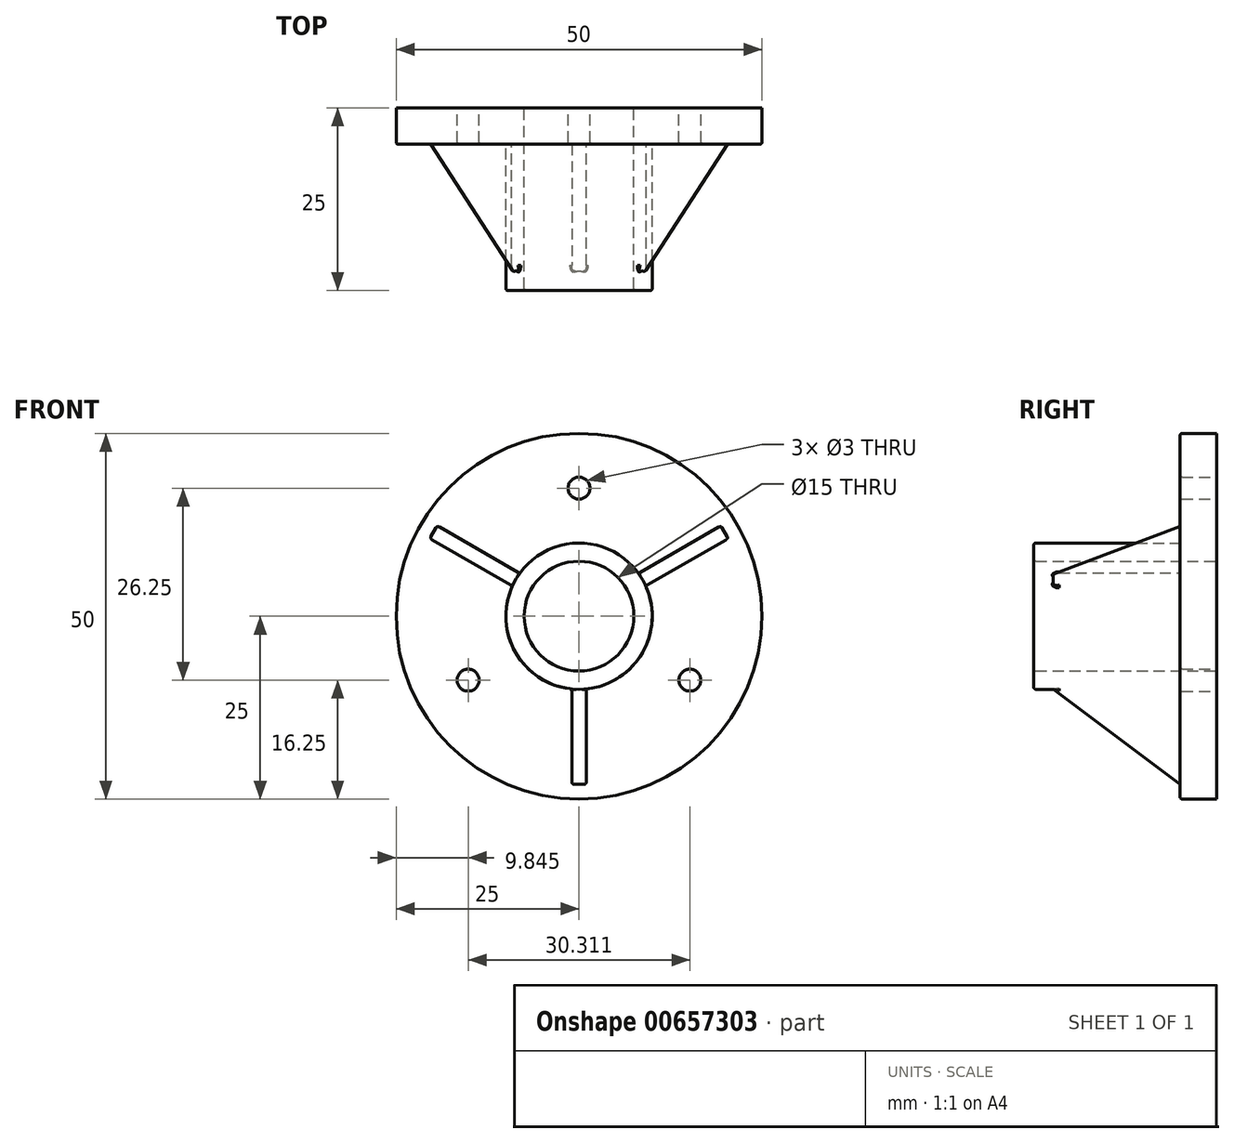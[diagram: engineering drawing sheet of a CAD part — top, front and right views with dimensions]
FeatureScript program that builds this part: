
annotation { "Feature Type Name" : "Feature", "Feature Type Description" : "" }
export const myFeature = defineFeature(function(context is Context, id is Id, definition is map)
    precondition{}
    {
        {
            var Q0;
            Q0=qCreatedBy(makeId("Front.planeOp"),FACE);
            var sketch = newSketch(context, id + "F0", { "sketchPlane" : qUnion([Q0])});
            skCircle(sketch, "E0", {"center": v(0, 0) * mm, "radius": 25 * mm});
            skCircle(sketch, "E1", {"center": v(0, 0) * mm, "radius": 10 * mm});
            skCircle(sketch, "E2", {"center": v(0, 17.5) * mm, "radius": 1.5 * mm});
            skCircle(sketch, "E3.1.0", {"center": v(-15.16, -8.75) * mm, "radius": 1.5 * mm});
            skCircle(sketch, "E3.2.0", {"center": v(15.16, -8.75) * mm, "radius": 1.5 * mm});
            skCircle(sketch, "E4", {"center": v(0, 0) * mm, "radius": 7.5 * mm});
            skSolve(sketch);
        }
        {
            var Q0;
            Q0 = qSketchRegion(id + "F0", true);
            extrude(context, id + "F1", {"entities" : qUnion([Q0]), "depth" : 5 * mm, "offsetDistance" : 25 * mm});
        }
        {
            var Q0;
            Q0=makeQuery(id+"F0.imprint","IMPRINT",FACE,{"disambiguationData":[TD([[makeQuery(id+"F0.imprint","IMPRINT",EDGE,{"derivedFrom":sQuery(id+"F0.wireOp",EDGE,"E1")}),1.0]])]});
            extrude(context, id + "F2", {"entities" : qUnion([Q0]), "operationType" : NewBodyOperationType.ADD, "depth" : 25 * mm, "offsetDistance" : 25 * mm});
        }
        {
            var Q0;
            Q0=qCreatedBy(makeId("Right.planeOp"),FACE);
            var sketch = newSketch(context, id + "F3", { "sketchPlane" : qUnion([Q0])});
            skLineSegment(sketch, "E5", {"start": v(7.15, 0) * mm, "end": v(-29.44, 0) * mm, "construction": true});
            skLineSegment(sketch, "E6", {"start": v(-25, -8) * mm, "end": v(-5, -8) * mm});
            skLineSegment(sketch, "E7", {"start": v(-5, -8) * mm, "end": v(-5, -23) * mm});
            skLineSegment(sketch, "E8", {"start": v(-5, -23) * mm, "end": v(-25, -8) * mm});
            skSolve(sketch);
        }
        {
            var Q0;
            Q0 = qSketchRegion(id + "F3", true);
            extrude(context, id + "F4", {"entities" : qUnion([Q0]), "endBound" : BoundingType.SYMMETRIC, "depth" : 2 * mm, "offsetDistance" : 25 * mm});
        }
        {
            var Q0;
            Q0=makeQuery(id+"F4.opExtrude","SWEPT_BODY",BODY,{"disambiguationData":[OSD([sQuery(id+"F3.wireOp",EDGE,"E6"),sQuery(id+"F3.wireOp",EDGE,"E7"),sQuery(id+"F3.wireOp",EDGE,"E8")])]});
            var Q1;
            Q1=sQuery(id+"F3.wireOp",EDGE,"E5");
            circularPattern(context, id + "F5", {"entities" : qUnion([Q0]), "axis" : qUnion([Q1]), "angle" : 360 * degree, "instanceCount" : 3, "equalSpace" : true});
        }
        {
            var Q0;
            Q0=makeQuery(id+"F5.opPattern","COPY",BODY,{"derivedFrom":makeQuery(id+"F4.opExtrude","SWEPT_BODY",BODY,{"disambiguationData":[OSD([sQuery(id+"F3.wireOp",EDGE,"E6"),sQuery(id+"F3.wireOp",EDGE,"E7"),sQuery(id+"F3.wireOp",EDGE,"E8")])]}),"instanceName":"2"});
            var Q1;
            Q1=makeQuery(id+"F5.opPattern","COPY",BODY,{"derivedFrom":makeQuery(id+"F4.opExtrude","SWEPT_BODY",BODY,{"disambiguationData":[OSD([sQuery(id+"F3.wireOp",EDGE,"E6"),sQuery(id+"F3.wireOp",EDGE,"E7"),sQuery(id+"F3.wireOp",EDGE,"E8")])]}),"instanceName":"1"});
            var Q2;
            Q2=makeQuery(id+"F4.opExtrude","SWEPT_BODY",BODY,{"disambiguationData":[OSD([sQuery(id+"F3.wireOp",EDGE,"E6"),sQuery(id+"F3.wireOp",EDGE,"E7"),sQuery(id+"F3.wireOp",EDGE,"E8")])]});
            var Q3;
            Q3=makeQuery(id+"F1.opExtrude","SWEPT_BODY",BODY,{"disambiguationData":[OSD([sQuery(id+"F0.wireOp",EDGE,"E0"),sQuery(id+"F0.wireOp",EDGE,"E1"),sQuery(id+"F0.wireOp",EDGE,"E2"),sQuery(id+"F0.wireOp",EDGE,"E3.1.0"),sQuery(id+"F0.wireOp",EDGE,"E3.2.0")])]});
            booleanBodies(context, id + "F6", {"operationType" : BooleanOperationType.UNION, "tools" : qUnion([Q0, Q1, Q2, Q3])});
        }
        {
            var Q0;
            {var subQ0=sQuery(id+"F0.wireOp",EDGE,"E1");var subQ1=sQuery(id+"F3.wireOp",EDGE,"E8");var subQ2=sQuery(id+"F3.wireOp",EDGE,"E7");var subQ3=sQuery(id+"F3.wireOp",EDGE,"E6");Q0=makeQuery(id+"F6.opBoolean","SPLIT",EDGE,{"disambiguationData":[TD([makeQuery(id+"F5.opPattern","COPY",FACE,{"derivedFrom":makeQuery(id+"F4.opExtrude","CAP_FACE",FACE,{"disambiguationData":[OSD([subQ3,subQ2,subQ1])],"isStart":false}),"instanceName":"1"})])],"derivedFrom":makeQuery(id+"F1.opExtrude","CAP_EDGE",EDGE,{"disambiguationData":[OSD([subQ0])],"isStart":false})});}
            var Q1;
            {var subQ0=sQuery(id+"F0.wireOp",EDGE,"E1");var subQ1=sQuery(id+"F3.wireOp",EDGE,"E8");var subQ2=sQuery(id+"F3.wireOp",EDGE,"E7");var subQ3=sQuery(id+"F3.wireOp",EDGE,"E6");Q1=makeQuery(id+"F6.opBoolean","SPLIT",EDGE,{"disambiguationData":[TD([makeQuery(id+"F4.opExtrude","CAP_FACE",FACE,{"disambiguationData":[OSD([subQ3,subQ2,subQ1])],"isStart":true})])],"derivedFrom":makeQuery(id+"F1.opExtrude","CAP_EDGE",EDGE,{"disambiguationData":[OSD([subQ0])],"isStart":false})});}
            var Q2;
            {var subQ0=sQuery(id+"F0.wireOp",EDGE,"E1");var subQ1=sQuery(id+"F3.wireOp",EDGE,"E8");var subQ2=sQuery(id+"F3.wireOp",EDGE,"E7");var subQ3=sQuery(id+"F3.wireOp",EDGE,"E6");Q2=makeQuery(id+"F6.opBoolean","SPLIT",EDGE,{"disambiguationData":[TD([makeQuery(id+"F4.opExtrude","CAP_FACE",FACE,{"disambiguationData":[OSD([subQ3,subQ2,subQ1])],"isStart":false})])],"derivedFrom":makeQuery(id+"F1.opExtrude","CAP_EDGE",EDGE,{"disambiguationData":[OSD([subQ0])],"isStart":false})});}
            var Q3;
            Q3=makeQuery(id+"F5.opPattern","COPY",EDGE,{"derivedFrom":makeQuery(id+"F4.opExtrude","CAP_EDGE",EDGE,{"disambiguationData":[OSD([sQuery(id+"F3.wireOp",EDGE,"E7")])],"isStart":true}),"instanceName":"2"});
            var Q4;
            Q4=makeQuery(id+"F5.opPattern","COPY",EDGE,{"derivedFrom":makeQuery(id+"F4.opExtrude","CAP_EDGE",EDGE,{"disambiguationData":[OSD([sQuery(id+"F3.wireOp",EDGE,"E7")])],"isStart":false}),"instanceName":"2"});
            var Q5;
            Q5=makeQuery(id+"F5.opPattern","COPY",EDGE,{"derivedFrom":makeQuery(id+"F4.opExtrude","CAP_EDGE",EDGE,{"disambiguationData":[OSD([sQuery(id+"F3.wireOp",EDGE,"E7")])],"isStart":false}),"instanceName":"1"});
            var Q6;
            Q6=makeQuery(id+"F5.opPattern","COPY",EDGE,{"derivedFrom":makeQuery(id+"F4.opExtrude","CAP_EDGE",EDGE,{"disambiguationData":[OSD([sQuery(id+"F3.wireOp",EDGE,"E7")])],"isStart":true}),"instanceName":"1"});
            var Q7;
            Q7=makeQuery(id+"F4.opExtrude","CAP_EDGE",EDGE,{"disambiguationData":[OSD([sQuery(id+"F3.wireOp",EDGE,"E7")])],"isStart":true});
            var Q8;
            Q8=makeQuery(id+"F4.opExtrude","CAP_EDGE",EDGE,{"disambiguationData":[OSD([sQuery(id+"F3.wireOp",EDGE,"E7")])],"isStart":false});
            var Q9;
            Q9=makeQuery(id+"F6.opBoolean","INTERSECT",EDGE,{"derivedFrom":[makeQuery(id+"F2.opExtrude","SWEPT_FACE",FACE,{"disambiguationData":[OSD([sQuery(id+"F0.wireOp",EDGE,"E1")])]}),makeQuery(id+"F5.opPattern","COPY",FACE,{"derivedFrom":makeQuery(id+"F4.opExtrude","CAP_FACE",FACE,{"disambiguationData":[OSD([sQuery(id+"F3.wireOp",EDGE,"E6"),sQuery(id+"F3.wireOp",EDGE,"E7"),sQuery(id+"F3.wireOp",EDGE,"E8")])],"isStart":true}),"instanceName":"1"})]});
            var Q10;
            Q10=makeQuery(id+"F6.opBoolean","INTERSECT",EDGE,{"derivedFrom":[makeQuery(id+"F2.opExtrude","SWEPT_FACE",FACE,{"disambiguationData":[OSD([sQuery(id+"F0.wireOp",EDGE,"E1")])]}),makeQuery(id+"F5.opPattern","COPY",FACE,{"derivedFrom":makeQuery(id+"F4.opExtrude","CAP_FACE",FACE,{"disambiguationData":[OSD([sQuery(id+"F3.wireOp",EDGE,"E6"),sQuery(id+"F3.wireOp",EDGE,"E7"),sQuery(id+"F3.wireOp",EDGE,"E8")])],"isStart":false}),"instanceName":"1"})]});
            var Q11;
            Q11=makeQuery(id+"F6.opBoolean","INTERSECT",EDGE,{"derivedFrom":[makeQuery(id+"F2.opExtrude","SWEPT_FACE",FACE,{"disambiguationData":[OSD([sQuery(id+"F0.wireOp",EDGE,"E1")])]}),makeQuery(id+"F5.opPattern","COPY",FACE,{"derivedFrom":makeQuery(id+"F4.opExtrude","CAP_FACE",FACE,{"disambiguationData":[OSD([sQuery(id+"F3.wireOp",EDGE,"E6"),sQuery(id+"F3.wireOp",EDGE,"E7"),sQuery(id+"F3.wireOp",EDGE,"E8")])],"isStart":true}),"instanceName":"2"})]});
            var Q12;
            Q12=makeQuery(id+"F6.opBoolean","INTERSECT",EDGE,{"derivedFrom":[makeQuery(id+"F2.opExtrude","SWEPT_FACE",FACE,{"disambiguationData":[OSD([sQuery(id+"F0.wireOp",EDGE,"E1")])]}),makeQuery(id+"F5.opPattern","COPY",FACE,{"derivedFrom":makeQuery(id+"F4.opExtrude","CAP_FACE",FACE,{"disambiguationData":[OSD([sQuery(id+"F3.wireOp",EDGE,"E6"),sQuery(id+"F3.wireOp",EDGE,"E7"),sQuery(id+"F3.wireOp",EDGE,"E8")])],"isStart":false}),"instanceName":"2"})]});
            var Q13;
            Q13=makeQuery(id+"F6.opBoolean","INTERSECT",EDGE,{"derivedFrom":[makeQuery(id+"F2.opExtrude","SWEPT_FACE",FACE,{"disambiguationData":[OSD([sQuery(id+"F0.wireOp",EDGE,"E1")])]}),makeQuery(id+"F4.opExtrude","CAP_FACE",FACE,{"disambiguationData":[OSD([sQuery(id+"F3.wireOp",EDGE,"E6"),sQuery(id+"F3.wireOp",EDGE,"E7"),sQuery(id+"F3.wireOp",EDGE,"E8")])],"isStart":true})]});
            var Q14;
            Q14=makeQuery(id+"F6.opBoolean","INTERSECT",EDGE,{"derivedFrom":[makeQuery(id+"F2.opExtrude","SWEPT_FACE",FACE,{"disambiguationData":[OSD([sQuery(id+"F0.wireOp",EDGE,"E1")])]}),makeQuery(id+"F4.opExtrude","CAP_FACE",FACE,{"disambiguationData":[OSD([sQuery(id+"F3.wireOp",EDGE,"E6"),sQuery(id+"F3.wireOp",EDGE,"E7"),sQuery(id+"F3.wireOp",EDGE,"E8")])],"isStart":false})]});
            var Q15;
            Q15=makeQuery(id+"F5.opPattern","COPY",EDGE,{"derivedFrom":makeQuery(id+"F4.opExtrude","CAP_EDGE",EDGE,{"disambiguationData":[OSD([sQuery(id+"F3.wireOp",EDGE,"E8")])],"isStart":false}),"instanceName":"1"});
            var Q16;
            Q16=makeQuery(id+"F5.opPattern","COPY",EDGE,{"derivedFrom":makeQuery(id+"F4.opExtrude","CAP_EDGE",EDGE,{"disambiguationData":[OSD([sQuery(id+"F3.wireOp",EDGE,"E8")])],"isStart":true}),"instanceName":"1"});
            var Q17;
            Q17=makeQuery(id+"F4.opExtrude","CAP_EDGE",EDGE,{"disambiguationData":[OSD([sQuery(id+"F3.wireOp",EDGE,"E8")])],"isStart":true});
            var Q18;
            Q18=makeQuery(id+"F4.opExtrude","CAP_EDGE",EDGE,{"disambiguationData":[OSD([sQuery(id+"F3.wireOp",EDGE,"E8")])],"isStart":false});
            var Q19;
            Q19=makeQuery(id+"F5.opPattern","COPY",EDGE,{"derivedFrom":makeQuery(id+"F4.opExtrude","CAP_EDGE",EDGE,{"disambiguationData":[OSD([sQuery(id+"F3.wireOp",EDGE,"E8")])],"isStart":true}),"instanceName":"2"});
            var Q20;
            Q20=makeQuery(id+"F5.opPattern","COPY",EDGE,{"derivedFrom":makeQuery(id+"F4.opExtrude","CAP_EDGE",EDGE,{"disambiguationData":[OSD([sQuery(id+"F3.wireOp",EDGE,"E8")])],"isStart":false}),"instanceName":"2"});
            var Q21;
            Q21=makeQuery(id+"F1.opExtrude","CAP_EDGE",EDGE,{"disambiguationData":[OSD([sQuery(id+"F0.wireOp",EDGE,"E3.1.0")])],"isStart":false});
            var Q22;
            Q22=makeQuery(id+"F1.opExtrude","CAP_EDGE",EDGE,{"disambiguationData":[OSD([sQuery(id+"F0.wireOp",EDGE,"E0")])],"isStart":false});
            var Q23;
            Q23=makeQuery(id+"F1.opExtrude","CAP_EDGE",EDGE,{"disambiguationData":[OSD([sQuery(id+"F0.wireOp",EDGE,"E2")])],"isStart":false});
            var Q24;
            Q24=makeQuery(id+"F1.opExtrude","CAP_EDGE",EDGE,{"disambiguationData":[OSD([sQuery(id+"F0.wireOp",EDGE,"E3.2.0")])],"isStart":false});
            var Q25;
            Q25=makeQuery(id+"F2.opExtrude","CAP_EDGE",EDGE,{"disambiguationData":[OSD([sQuery(id+"F0.wireOp",EDGE,"E4")])],"isStart":false});
            var Q26;
            Q26=makeQuery(id+"F2.opExtrude","CAP_EDGE",EDGE,{"disambiguationData":[OSD([sQuery(id+"F0.wireOp",EDGE,"E1")])],"isStart":false});
            fillet(context, id + "F7", {"entities" : qUnion([Q0, Q1, Q2, Q3, Q4, Q5, Q6, Q7, Q8, Q9, Q10, Q11, Q12, Q13, Q14, Q15, Q16, Q17, Q18, Q19, Q20, Q21, Q22, Q23, Q24, Q25, Q26]), "radius" : 0.3 * mm, "tangentPropagation" : true, "allowEdgeOverflow" : false});
        }
    });
